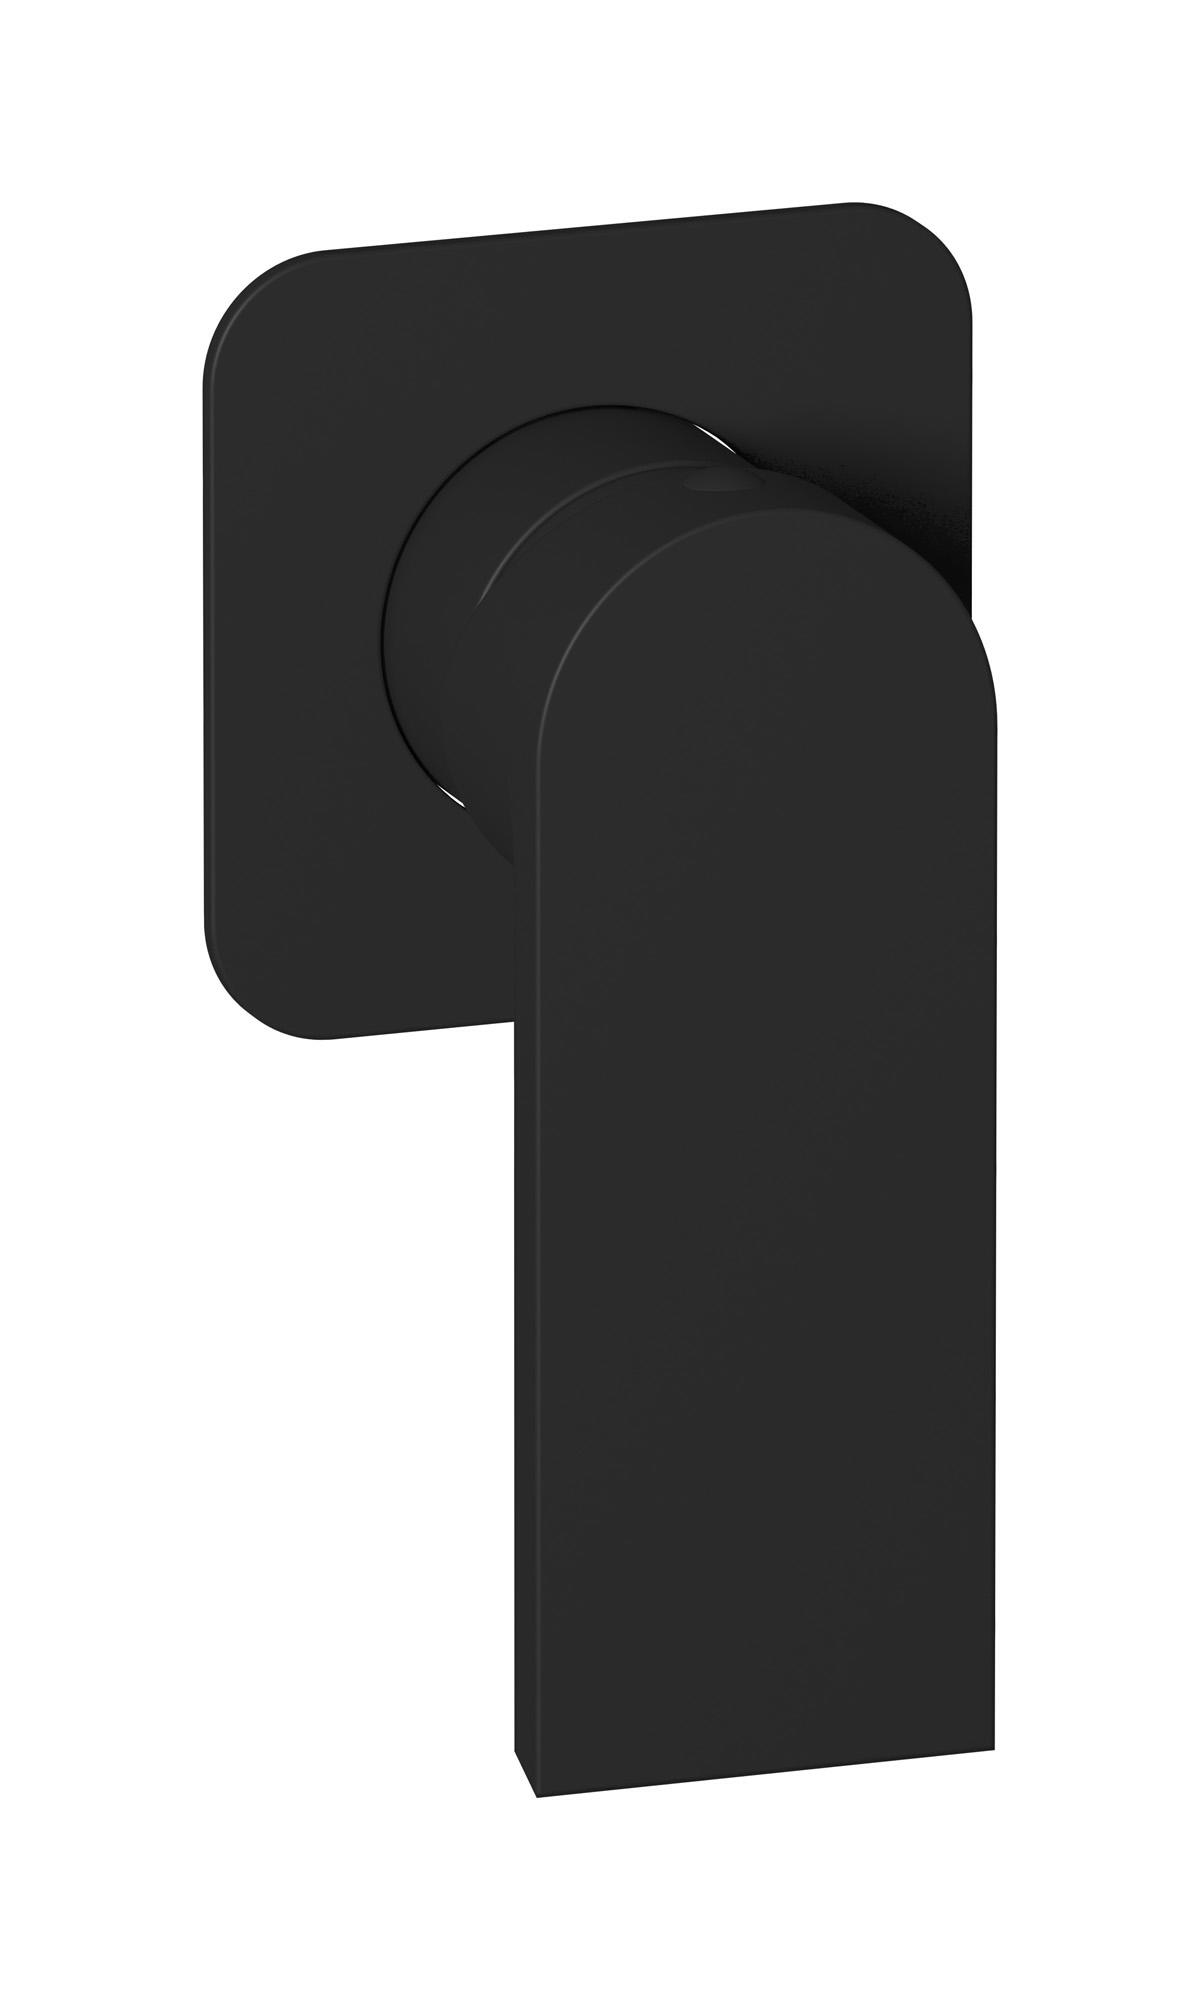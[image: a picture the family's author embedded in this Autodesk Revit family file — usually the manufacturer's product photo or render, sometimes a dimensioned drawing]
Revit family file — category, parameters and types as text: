
# Revit family: K3300
name_source: partatom
category: Apparecchi idraulici
units: mm (PartAtom-declared; Revit-internal decimal feet)

## family parameters
Basato su piano di lavoro = No
Condiviso = No
Mantieni orientamento annotazione = No
Numero OmniClass = 23.45.55.17
Punto di calcolo locali = No
Quota connettore circolare = Usa diametro
Sempre verticale = Sì
Taglio con vuoti quando caricato = No
Tipo di parte = Normale
Titolo OmniClass = Mixing Faucets

## types (8) — shared parameters
Cold water inlet = 10 mm  [stored 0.0328084 ft]
Commenti sul tipo = Wall mixer
Connessione CW = No
Connessione HW = No
Connessione di scarico = No
Connessione di ventilazione = No
Descrizione = Exposed parts for manual wall mixer
Hot water inlet = 10 mm  [stored 0.0328084 ft]
Produttore = IB Rubinetterie S.p.A.
URL = https://www.weareib.it
zero-valued in all types: Prospetto di default

## per-type parameters (varying)
| type | Finishes surface | Immagine tipo | Modello |
| Chrome | IB_Chrome | K3300CC.jpg | K3300CC |
| Brushed nickel | IB_Brushed nickel | K3300SS.jpg | K3300SS |
| Matt black | IB_matt black | K3300NP.jpg | K3300NP |
| Matt white | IB_matt white | K3300BO.jpg | K3300BO |
| Pale gold | IB_Pale gold | K3300II.jpg | K3300II |
| Brushed pale gold | IB_brushed pale gold | K3300IS.jpg | K3300IS |
| Rose gold | IB_Rose gold | K3300RS.jpg | K3300RS |
| Gold | IB_gold | K3300OO.jpg | K3300OO |

note: [stored X ft] marks values corroborated as IEEE doubles in the binary element streams (Revit-internal decimal feet)
